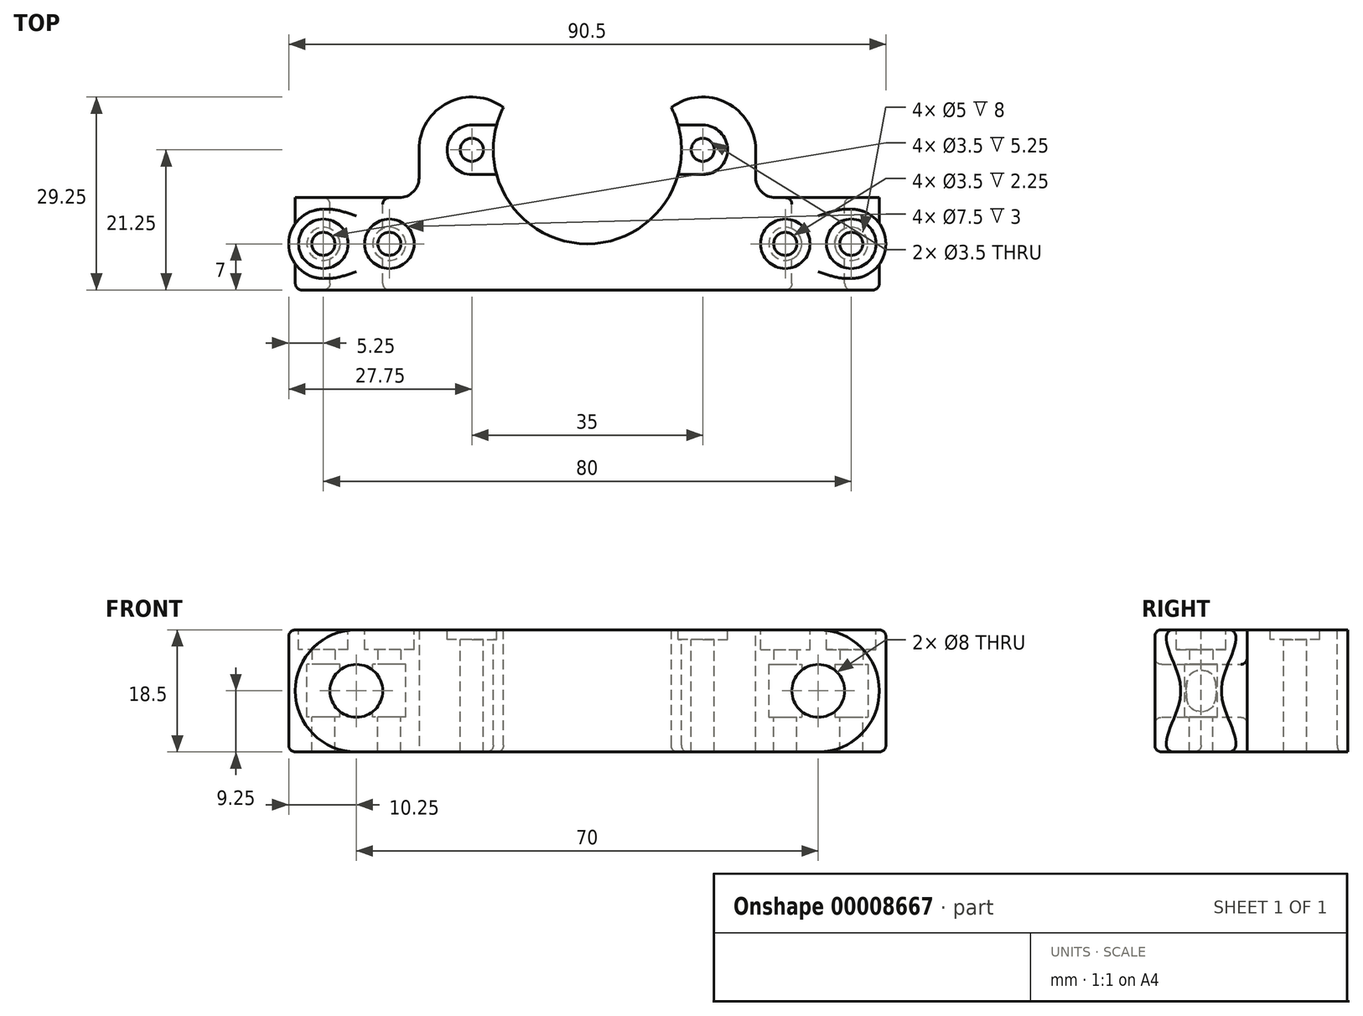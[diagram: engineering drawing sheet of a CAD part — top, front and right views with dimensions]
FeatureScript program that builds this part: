
annotation { "Feature Type Name" : "Feature", "Feature Type Description" : "" }
export const myFeature = defineFeature(function(context is Context, id is Id, definition is map)
    precondition{}
    {
        {
            var Q0;
            Q0=qCreatedBy(makeId("Front.planeOp"),FACE);
            var sketch = newSketch(context, id + "F0", { "sketchPlane" : qUnion([Q0])});
            skCircle(sketch, "E0", {"center": v(-35, 0) * mm, "radius": 4 * mm});
            skCircle(sketch, "E1", {"center": v(-35, 0) * mm, "radius": 9.25 * mm});
            skLineSegment(sketch, "E2", {"start": v(-44.25, 0) * mm, "end": v(0, 0) * mm});
            skLineSegment(sketch, "E3", {"start": v(-35, 9.25) * mm, "end": v(0, 9.25) * mm});
            skLineSegment(sketch, "E4", {"start": v(0, 0) * mm, "end": v(0, 9.25) * mm});
            skCircle(sketch, "E5", {"center": v(-6, 0) * mm, "radius": 2.75 * mm});
            skPoint(sketch, "E6", {"position": v(-35, -9.25) * mm});
            skSolve(sketch);
        }
        {
            var Q0;
            {var subQ0=sQuery(id+"F0.wireOp",EDGE,"E2");var subQ1=sQuery(id+"F0.wireOp",EDGE,"E0");var subQ2=makeQuery(id+"F0.imprint","INTERSECT",VERTEX,{"disambiguationData":[OD(0.0)],"derivedFrom":[subQ1,subQ0]});Q0=makeQuery(id+"F0.imprint","IMPRINT",FACE,{"disambiguationData":[TD([[makeQuery(id+"F0.imprint","IMPRINT",EDGE,{"disambiguationData":[TD([[subQ2,1.0]])],"derivedFrom":subQ1}),-1.0]])]});}
            var Q1;
            {var subQ1=sQuery(id+"F0.wireOp",EDGE,"E3");Q1=makeQuery(id+"F0.imprint","IMPRINT",FACE,{"disambiguationData":[TD([[makeQuery(id+"F0.imprint","IMPRINT",EDGE,{"derivedFrom":subQ1}),-1.0]])]});}
            var Q2;
            {var subQ0=sQuery(id+"F0.wireOp",EDGE,"E2");var subQ1=sQuery(id+"F0.wireOp",EDGE,"E0");var subQ3=makeQuery(id+"F0.imprint","INTERSECT",VERTEX,{"disambiguationData":[OD(0.0)],"derivedFrom":[subQ1,subQ0]});Q2=makeQuery(id+"F0.imprint","IMPRINT",FACE,{"disambiguationData":[TD([[makeQuery(id+"F0.imprint","IMPRINT",EDGE,{"disambiguationData":[TD([[subQ3,1.0]])],"derivedFrom":subQ1}),1.0]])]});}
            var Q3;
            {var subQ0=sQuery(id+"F0.wireOp",EDGE,"E5");var subQ1=sQuery(id+"F0.wireOp",EDGE,"E2");var subQ3=makeQuery(id+"F0.imprint","INTERSECT",VERTEX,{"disambiguationData":[OD(0.0)],"derivedFrom":[subQ1,subQ0]});Q3=makeQuery(id+"F0.imprint","IMPRINT",FACE,{"disambiguationData":[TD([[makeQuery(id+"F0.imprint","IMPRINT",EDGE,{"disambiguationData":[TD([[subQ3,-1.0]])],"derivedFrom":subQ1}),1.0]])]});}
            extrude(context, id + "F1", {"entities" : qUnion([Q0, Q1, Q2, Q3]), "depth" : 14 * mm, "symmetric" : true});
        }
        {
            var Q0;
            Q0=qCreatedBy(makeId("Top.planeOp"),FACE);
            var sketch = newSketch(context, id + "F2", { "sketchPlane" : qUnion([Q0])});
            skLineSegment(sketch, "E7.0", {"start": v(-31, 0) * mm, "end": v(-39, 0) * mm, "construction": true});
            skLineSegment(sketch, "E8.0", {"start": v(-35, 7) * mm, "end": v(-44.25, 7) * mm, "construction": true});
            skLineSegment(sketch, "E9.0", {"start": v(-35, -7) * mm, "end": v(-44.25, -7) * mm, "construction": true});
            skLineSegment(sketch, "E10.0", {"start": v(-35, -7) * mm, "end": v(0, -7) * mm, "construction": true});
            skLineSegment(sketch, "E11.0", {"start": v(-35, 7) * mm, "end": v(0, 7) * mm, "construction": true});
            skLineSegment(sketch, "E12", {"start": v(-39, 7) * mm, "end": v(-39, -7) * mm, "construction": true});
            skLineSegment(sketch, "E13", {"start": v(-31, 7) * mm, "end": v(-31, -7) * mm, "construction": true});
            skLineSegment(sketch, "E14", {"start": v(-35, 7) * mm, "end": v(-35, -7) * mm, "construction": true});
            skCircle(sketch, "E15", {"center": v(-40, 0) * mm, "radius": 1.75 * mm});
            skCircle(sketch, "E16", {"center": v(-30, 0) * mm, "radius": 1.75 * mm});
            skCircle(sketch, "E17", {"center": v(-30, 0) * mm, "radius": 2.5 * mm});
            skCircle(sketch, "E18", {"center": v(-40, 0) * mm, "radius": 2.5 * mm});
            skPoint(sketch, "E19", {"position": v(-38.25, 0) * mm});
            skCircle(sketch, "E20", {"center": v(-40, 0) * mm, "radius": 5.25 * mm});
            skCircle(sketch, "E21", {"center": v(-30, 0) * mm, "radius": 5.25 * mm});
            skCircle(sketch, "E22", {"center": v(-40, 0) * mm, "radius": 3.75 * mm});
            skCircle(sketch, "E23", {"center": v(-30, 0) * mm, "radius": 3.75 * mm});
            skLineSegment(sketch, "E24", {"start": v(-40, -5.25) * mm, "end": v(-35, -5.25) * mm});
            skLineSegment(sketch, "E25", {"start": v(-40, 5.25) * mm, "end": v(-35, 5.25) * mm});
            skLineSegment(sketch, "E26", {"start": v(-35, 5.25) * mm, "end": v(-35, -5.25) * mm});
            skSolve(sketch);
        }
        {
            var Q0;
            Q0=makeQuery(id+"F2.imprint","IMPRINT",FACE,{"disambiguationData":[TD([[makeQuery(id+"F2.imprint","IMPRINT",EDGE,{"derivedFrom":sQuery(id+"F2.wireOp",EDGE,"E20")}),1.0]])]});
            var Q1;
            Q1=makeQuery(id+"F2.imprint","IMPRINT",FACE,{"disambiguationData":[TD([[makeQuery(id+"F2.imprint","IMPRINT",EDGE,{"derivedFrom":sQuery(id+"F2.wireOp",EDGE,"E21")}),1.0]])]});
            var Q2;
            Q2=makeQuery(id+"F2.imprint","IMPRINT",FACE,{"disambiguationData":[TD([[makeQuery(id+"F2.imprint","IMPRINT",EDGE,{"derivedFrom":sQuery(id+"F2.wireOp",EDGE,"E18")}),-1.0]])]});
            var Q3;
            Q3=makeQuery(id+"F2.imprint","IMPRINT",FACE,{"disambiguationData":[TD([[makeQuery(id+"F2.imprint","IMPRINT",EDGE,{"derivedFrom":sQuery(id+"F2.wireOp",EDGE,"E15")}),-1.0]])]});
            var Q4;
            Q4=makeQuery(id+"F2.imprint","IMPRINT",FACE,{"disambiguationData":[TD([[makeQuery(id+"F2.imprint","IMPRINT",EDGE,{"derivedFrom":sQuery(id+"F2.wireOp",EDGE,"E15")}),1.0]])]});
            var Q5;
            Q5=makeQuery(id+"F2.imprint","IMPRINT",FACE,{"disambiguationData":[TD([[makeQuery(id+"F2.imprint","IMPRINT",EDGE,{"derivedFrom":sQuery(id+"F2.wireOp",EDGE,"E16")}),1.0]])]});
            var Q6;
            Q6=makeQuery(id+"F2.imprint","IMPRINT",FACE,{"disambiguationData":[TD([[makeQuery(id+"F2.imprint","IMPRINT",EDGE,{"derivedFrom":sQuery(id+"F2.wireOp",EDGE,"E16")}),-1.0]])]});
            var Q7;
            Q7=makeQuery(id+"F2.imprint","IMPRINT",FACE,{"disambiguationData":[TD([[makeQuery(id+"F2.imprint","IMPRINT",EDGE,{"derivedFrom":sQuery(id+"F2.wireOp",EDGE,"E17")}),-1.0]])]});
            var Q8;
            {var subQ3=sQuery(id+"F2.wireOp",EDGE,"E24");Q8=makeQuery(id+"F2.imprint","IMPRINT",FACE,{"disambiguationData":[TD([[makeQuery(id+"F2.imprint","IMPRINT",EDGE,{"derivedFrom":subQ3}),1.0]])]});}
            var Q9;
            {var subQ3=sQuery(id+"F2.wireOp",EDGE,"E25");Q9=makeQuery(id+"F2.imprint","IMPRINT",FACE,{"disambiguationData":[TD([[makeQuery(id+"F2.imprint","IMPRINT",EDGE,{"derivedFrom":subQ3}),-1.0]])]});}
            var Q10;
            Q10=makeQuery(id+"F1.opExtrude","SWEPT_FACE",FACE,{"disambiguationData":[OSD([sQuery(id+"F0.wireOp",EDGE,"E3")])]});
            extrude(context, id + "F3", {"entities" : qUnion([Q0, Q1, Q2, Q3, Q4, Q5, Q6, Q7, Q8, Q9]), "operationType" : NewBodyOperationType.ADD, "endBound" : BoundingType.UP_TO_SURFACE, "endBoundEntityFace" : qUnion([Q10]), "depth" : 8.5 * mm});
        }
        {
            var Q0;
            Q0=makeQuery(id+"F2.imprint","IMPRINT",FACE,{"disambiguationData":[TD([[makeQuery(id+"F2.imprint","IMPRINT",EDGE,{"derivedFrom":sQuery(id+"F2.wireOp",EDGE,"E15")}),1.0]])]});
            var Q1;
            Q1=makeQuery(id+"F2.imprint","IMPRINT",FACE,{"disambiguationData":[TD([[makeQuery(id+"F2.imprint","IMPRINT",EDGE,{"derivedFrom":sQuery(id+"F2.wireOp",EDGE,"E16")}),1.0]])]});
            extrude(context, id + "F4", {"entities" : qUnion([Q0, Q1]), "operationType" : NewBodyOperationType.REMOVE, "depth" : 25 * mm});
        }
        {
            var Q0;
            Q0=makeQuery(id+"F2.imprint","IMPRINT",FACE,{"disambiguationData":[TD([[makeQuery(id+"F2.imprint","IMPRINT",EDGE,{"derivedFrom":sQuery(id+"F2.wireOp",EDGE,"E15")}),-1.0]])]});
            var Q1;
            Q1=makeQuery(id+"F2.imprint","IMPRINT",FACE,{"disambiguationData":[TD([[makeQuery(id+"F2.imprint","IMPRINT",EDGE,{"derivedFrom":sQuery(id+"F2.wireOp",EDGE,"E15")}),1.0]])]});
            var Q2;
            Q2=makeQuery(id+"F2.imprint","IMPRINT",FACE,{"disambiguationData":[TD([[makeQuery(id+"F2.imprint","IMPRINT",EDGE,{"derivedFrom":sQuery(id+"F2.wireOp",EDGE,"E16")}),1.0]])]});
            var Q3;
            Q3=makeQuery(id+"F2.imprint","IMPRINT",FACE,{"disambiguationData":[TD([[makeQuery(id+"F2.imprint","IMPRINT",EDGE,{"derivedFrom":sQuery(id+"F2.wireOp",EDGE,"E16")}),-1.0]])]});
            extrude(context, id + "F5", {"entities" : qUnion([Q0, Q1, Q2, Q3]), "operationType" : NewBodyOperationType.REMOVE, "depth" : 4 * mm});
        }
        {
            var Q0;
            {var subQ0=sQuery(id+"F0.wireOp",EDGE,"E2");var subQ1=sQuery(id+"F0.wireOp",EDGE,"E0");var subQ3=makeQuery(id+"F0.imprint","INTERSECT",VERTEX,{"disambiguationData":[OD(0.0)],"derivedFrom":[subQ1,subQ0]});Q0=makeQuery(id+"F0.imprint","IMPRINT",FACE,{"disambiguationData":[TD([[makeQuery(id+"F0.imprint","IMPRINT",EDGE,{"disambiguationData":[TD([[subQ3,1.0]])],"derivedFrom":subQ1}),1.0]])]});}
            extrude(context, id + "F6", {"entities" : qUnion([Q0]), "operationType" : NewBodyOperationType.REMOVE, "depth" : 25 * mm, "symmetric" : true});
        }
        {
            var Q0;
            Q0=makeQuery(id+"F1.opExtrude","SWEPT_BODY",BODY,{"disambiguationData":[OSD([sQuery(id+"F0.wireOp",EDGE,"E1"),sQuery(id+"F0.wireOp",EDGE,"E2"),sQuery(id+"F0.wireOp",EDGE,"E3"),sQuery(id+"F0.wireOp",EDGE,"E4")])]});
            var Q1;
            Q1=qCreatedBy(makeId("Top.planeOp"),FACE);
            mirror(context, id + "F7", {"entities" : qUnion([Q0]), "mirrorPlane" : qUnion([Q1])});
        }
        {
            var Q0;
            Q0=makeQuery(id+"F1.opExtrude","SWEPT_FACE",FACE,{"disambiguationData":[OSD([sQuery(id+"F0.wireOp",EDGE,"E3")])]});
            var sketch = newSketch(context, id + "F8", { "sketchPlane" : qUnion([Q0])});
            skCircle(sketch, "E27.0.0", {"center": v(-40, 0) * mm, "radius": 5.25 * mm});
            skCircle(sketch, "E28.0", {"center": v(-30, 0) * mm, "radius": 1.75 * mm});
            skCircle(sketch, "E29", {"center": v(-30, 0) * mm, "radius": 3.75 * mm});
            skCircle(sketch, "E30", {"center": v(-40, 0) * mm, "radius": 3.75 * mm});
            skSolve(sketch);
        }
        {
            var Q0;
            Q0=makeQuery(id+"F8.imprint","IMPRINT",FACE,{"disambiguationData":[TD([[makeQuery(id+"F8.imprint","IMPRINT",EDGE,{"derivedFrom":sQuery(id+"F8.wireOp",EDGE,"E30")}),1.0]])]});
            var Q1;
            Q1=makeQuery(id+"F8.imprint","IMPRINT",FACE,{"disambiguationData":[TD([[makeQuery(id+"F8.imprint","IMPRINT",EDGE,{"derivedFrom":sQuery(id+"F8.wireOp",EDGE,"E28.0")}),1.0]])]});
            extrude(context, id + "F9", {"entities" : qUnion([Q0, Q1]), "operationType" : NewBodyOperationType.REMOVE, "oppositeDirection" : true, "depth" : 3 * mm});
        }
        {
            var Q0;
            Q0=makeQuery(id+"F1.opExtrude","SWEPT_BODY",BODY,{"disambiguationData":[OSD([sQuery(id+"F0.wireOp",EDGE,"E1"),sQuery(id+"F0.wireOp",EDGE,"E2"),sQuery(id+"F0.wireOp",EDGE,"E3"),sQuery(id+"F0.wireOp",EDGE,"E4")])]});
            var Q1;
            Q1=makeQuery(id+"F7.opPattern","COPY",BODY,{"derivedFrom":makeQuery(id+"F1.opExtrude","SWEPT_BODY",BODY,{"disambiguationData":[OSD([sQuery(id+"F0.wireOp",EDGE,"E1"),sQuery(id+"F0.wireOp",EDGE,"E2"),sQuery(id+"F0.wireOp",EDGE,"E3"),sQuery(id+"F0.wireOp",EDGE,"E4")])]}),"instanceName":"1"});
            var Q2;
            Q2=qCreatedBy(makeId("Right.planeOp"),FACE);
            mirror(context, id + "F10", {"entities" : qUnion([Q0, Q1]), "mirrorPlane" : qUnion([Q2])});
        }
        {
            var Q0;
            Q0=makeQuery(id+"F7.opPattern","COPY",BODY,{"derivedFrom":makeQuery(id+"F1.opExtrude","SWEPT_BODY",BODY,{"disambiguationData":[OSD([sQuery(id+"F0.wireOp",EDGE,"E1"),sQuery(id+"F0.wireOp",EDGE,"E2"),sQuery(id+"F0.wireOp",EDGE,"E3"),sQuery(id+"F0.wireOp",EDGE,"E4")])]}),"instanceName":"1"});
            var Q1;
            Q1=makeQuery(id+"F10.opPattern","COPY",BODY,{"derivedFrom":makeQuery(id+"F1.opExtrude","SWEPT_BODY",BODY,{"disambiguationData":[OSD([sQuery(id+"F0.wireOp",EDGE,"E1"),sQuery(id+"F0.wireOp",EDGE,"E2"),sQuery(id+"F0.wireOp",EDGE,"E3"),sQuery(id+"F0.wireOp",EDGE,"E4")])]}),"instanceName":"1"});
            var Q2;
            Q2=makeQuery(id+"F1.opExtrude","SWEPT_BODY",BODY,{"disambiguationData":[OSD([sQuery(id+"F0.wireOp",EDGE,"E1"),sQuery(id+"F0.wireOp",EDGE,"E2"),sQuery(id+"F0.wireOp",EDGE,"E3"),sQuery(id+"F0.wireOp",EDGE,"E4")])]});
            var Q3;
            Q3=makeQuery(id+"F10.opPattern","COPY",BODY,{"derivedFrom":makeQuery(id+"F7.opPattern","COPY",BODY,{"derivedFrom":makeQuery(id+"F1.opExtrude","SWEPT_BODY",BODY,{"disambiguationData":[OSD([sQuery(id+"F0.wireOp",EDGE,"E1"),sQuery(id+"F0.wireOp",EDGE,"E2"),sQuery(id+"F0.wireOp",EDGE,"E3"),sQuery(id+"F0.wireOp",EDGE,"E4")])]}),"instanceName":"1"}),"instanceName":"1"});
            booleanBodies(context, id + "F11", {"operationType" : BooleanOperationType.UNION, "tools" : qUnion([Q0, Q1, Q2, Q3])});
        }
        {
            var Q0;
            {var subQ0=sQuery(id+"F0.wireOp",EDGE,"E3");var subQ1=makeQuery(id+"F3.boolean.opBoolean","MERGE",FACE,{"derivedFrom":[makeQuery(id+"F1.opExtrude","SWEPT_FACE",FACE,{"disambiguationData":[OSD([subQ0])]}),makeQuery(id+"F3.opExtrude","CAP_FACE",FACE,{"disambiguationData":[OSD([subQ0]),ownerDisambiguation([makeQuery(id+"F3.opExtrude","SWEPT_BODY",BODY,{"disambiguationData":[OSD([sQuery(id+"F2.wireOp",EDGE,"E20"),sQuery(id+"F2.wireOp",EDGE,"E24"),sQuery(id+"F2.wireOp",EDGE,"E25"),sQuery(id+"F2.wireOp",EDGE,"E26")])]})])],"isStart":false})]});Q0=makeQuery(id+"F11.opBoolean","MERGE",FACE,{"derivedFrom":[subQ1,makeQuery(id+"F10.opPattern","COPY",FACE,{"derivedFrom":subQ1,"instanceName":"1"})]});}
            var sketch = newSketch(context, id + "F12", { "sketchPlane" : qUnion([Q0])});
            skCircle(sketch, "E31", {"center": v(-17.5, 14.25) * mm, "radius": 1.75 * mm});
            skCircle(sketch, "E32", {"center": v(17.5, 14.25) * mm, "radius": 1.75 * mm});
            skCircle(sketch, "E33", {"center": v(-17.5, 14.25) * mm, "radius": 3.75 * mm});
            skCircle(sketch, "E34", {"center": v(17.5, 14.25) * mm, "radius": 3.75 * mm});
            skCircle(sketch, "E35", {"center": v(0, 14.25) * mm, "radius": 14.25 * mm});
            skCircle(sketch, "E36", {"center": v(-17.5, 14.25) * mm, "radius": 8 * mm});
            skCircle(sketch, "E37", {"center": v(17.5, 14.25) * mm, "radius": 8 * mm});
            skLineSegment(sketch, "E38", {"start": v(-25.5, 14.25) * mm, "end": v(25.5, 14.25) * mm, "construction": true});
            skLineSegment(sketch, "E39", {"start": v(-25.5, 14.25) * mm, "end": v(-25.5, 0) * mm});
            skLineSegment(sketch, "E40", {"start": v(-25.5, 0) * mm, "end": v(25.5, 0) * mm});
            skLineSegment(sketch, "E41", {"start": v(25.5, 0) * mm, "end": v(25.5, 14.25) * mm});
            skLineSegment(sketch, "E42", {"start": v(-17.5, 22.25) * mm, "end": v(17.5, 22.25) * mm});
            skLineSegment(sketch, "E43", {"start": v(-17.5, 18) * mm, "end": v(17.5, 18) * mm});
            skLineSegment(sketch, "E44", {"start": v(17.5, 10.5) * mm, "end": v(-17.5, 10.5) * mm});
            skPoint(sketch, "E45", {"position": v(-11.8, 22.25) * mm});
            skPoint(sketch, "E46", {"position": v(11.8, 22.25) * mm});
            skSolve(sketch);
        }
        {
            var Q0;
            {var subQ7=sQuery(id+"F12.wireOp",EDGE,"E41");var subQ9=sQuery(id+"F12.wireOp",EDGE,"E40");var subQ10=makeQuery(id+"F12.imprint","INTERSECT",VERTEX,{"derivedFrom":[subQ9,subQ7]});Q0=makeQuery(id+"F12.imprint","IMPRINT",FACE,{"disambiguationData":[TD([[makeQuery(id+"F12.imprint","IMPRINT",EDGE,{"disambiguationData":[TD([[subQ10,1.0]])],"derivedFrom":subQ9}),1.0]])]});}
            var Q1;
            {var subQ0=sQuery(id+"F12.wireOp",EDGE,"E44");var subQ3=sQuery(id+"F12.wireOp",EDGE,"E35");var subQ4=makeQuery(id+"F12.imprint","INTERSECT",VERTEX,{"disambiguationData":[OD(0.0)],"derivedFrom":[subQ3,subQ0]});Q1=makeQuery(id+"F12.imprint","IMPRINT",FACE,{"disambiguationData":[TD([[makeQuery(id+"F12.imprint","IMPRINT",EDGE,{"disambiguationData":[TD([[subQ4,-1.0]])],"derivedFrom":subQ3}),1.0]])]});}
            var Q2;
            {var subQ0=sQuery(id+"F12.wireOp",EDGE,"E43");var subQ3=sQuery(id+"F12.wireOp",EDGE,"E33");var subQ4=makeQuery(id+"F12.imprint","INTERSECT",VERTEX,{"derivedFrom":[subQ3,subQ0]});Q2=makeQuery(id+"F12.imprint","IMPRINT",FACE,{"disambiguationData":[TD([[makeQuery(id+"F12.imprint","IMPRINT",EDGE,{"disambiguationData":[TD([[subQ4,1.0]])],"derivedFrom":subQ3}),-1.0]])]});}
            var Q3;
            {var subQ0=sQuery(id+"F12.wireOp",EDGE,"E42");var subQ1=sQuery(id+"F12.wireOp",EDGE,"E35");var subQ2=makeQuery(id+"F12.imprint","INTERSECT",VERTEX,{"disambiguationData":[OD(1.0)],"derivedFrom":[subQ1,subQ0]});Q3=makeQuery(id+"F12.imprint","IMPRINT",FACE,{"disambiguationData":[TD([[makeQuery(id+"F12.imprint","IMPRINT",EDGE,{"disambiguationData":[TD([[subQ2,-1.0]])],"derivedFrom":subQ1}),-1.0]])]});}
            var Q4;
            {var subQ0=sQuery(id+"F12.wireOp",EDGE,"E44");var subQ3=sQuery(id+"F12.wireOp",EDGE,"E34");var subQ4=makeQuery(id+"F12.imprint","INTERSECT",VERTEX,{"derivedFrom":[subQ3,subQ0]});Q4=makeQuery(id+"F12.imprint","IMPRINT",FACE,{"disambiguationData":[TD([[makeQuery(id+"F12.imprint","IMPRINT",EDGE,{"disambiguationData":[TD([[subQ4,1.0]])],"derivedFrom":subQ3}),-1.0]])]});}
            var Q5;
            {var subQ3=sQuery(id+"F12.wireOp",EDGE,"E35");var subQ8=sQuery(id+"F12.wireOp",EDGE,"E33");var subQ10=makeQuery(id+"F12.imprint","INTERSECT",VERTEX,{"disambiguationData":[OD(0.0)],"derivedFrom":[subQ8,subQ3]});Q5=makeQuery(id+"F12.imprint","IMPRINT",FACE,{"disambiguationData":[TD([[makeQuery(id+"F12.imprint","IMPRINT",EDGE,{"disambiguationData":[TD([[subQ10,1.0]])],"derivedFrom":subQ8}),-1.0]])]});}
            var Q6;
            {var subQ0=sQuery(id+"F12.wireOp",EDGE,"E44");var subQ3=sQuery(id+"F12.wireOp",EDGE,"E33");var subQ4=makeQuery(id+"F12.imprint","INTERSECT",VERTEX,{"derivedFrom":[subQ3,subQ0]});Q6=makeQuery(id+"F12.imprint","IMPRINT",FACE,{"disambiguationData":[TD([[makeQuery(id+"F12.imprint","IMPRINT",EDGE,{"disambiguationData":[TD([[subQ4,-1.0]])],"derivedFrom":subQ3}),-1.0]])]});}
            var Q7;
            {var subQ8=sQuery(id+"F12.wireOp",EDGE,"E33");var subQ10=sQuery(id+"F12.wireOp",EDGE,"E43");var subQ12=makeQuery(id+"F12.imprint","INTERSECT",VERTEX,{"derivedFrom":[subQ8,subQ10]});Q7=makeQuery(id+"F12.imprint","IMPRINT",FACE,{"disambiguationData":[TD([[makeQuery(id+"F12.imprint","IMPRINT",EDGE,{"disambiguationData":[TD([[subQ12,-1.0]])],"derivedFrom":subQ8}),-1.0]])]});}
            var Q8;
            Q8=makeQuery(id+"F12.imprint","IMPRINT",FACE,{"disambiguationData":[TD([[makeQuery(id+"F12.imprint","IMPRINT",EDGE,{"derivedFrom":sQuery(id+"F12.wireOp",EDGE,"E31")}),-1.0]])]});
            var Q9;
            {var subQ3=sQuery(id+"F12.wireOp",EDGE,"E35");var subQ8=sQuery(id+"F12.wireOp",EDGE,"E34");var subQ10=makeQuery(id+"F12.imprint","INTERSECT",VERTEX,{"disambiguationData":[OD(0.0)],"derivedFrom":[subQ8,subQ3]});Q9=makeQuery(id+"F12.imprint","IMPRINT",FACE,{"disambiguationData":[TD([[makeQuery(id+"F12.imprint","IMPRINT",EDGE,{"disambiguationData":[TD([[subQ10,-1.0]])],"derivedFrom":subQ8}),-1.0]])]});}
            var Q10;
            {var subQ5=sQuery(id+"F12.wireOp",EDGE,"E42");var subQ6=sQuery(id+"F12.wireOp",EDGE,"E35");var subQ8=makeQuery(id+"F12.imprint","INTERSECT",VERTEX,{"disambiguationData":[OD(0.0)],"derivedFrom":[subQ6,subQ5]});Q10=makeQuery(id+"F12.imprint","IMPRINT",FACE,{"disambiguationData":[TD([[makeQuery(id+"F12.imprint","IMPRINT",EDGE,{"disambiguationData":[TD([[subQ8,1.0]])],"derivedFrom":subQ6}),1.0]])]});}
            var Q11;
            {var subQ2=sQuery(id+"F12.wireOp",EDGE,"E37");var subQ4=sQuery(id+"F12.wireOp",EDGE,"E35");var subQ6=makeQuery(id+"F12.imprint","INTERSECT",VERTEX,{"disambiguationData":[OD(1.0)],"derivedFrom":[subQ4,subQ2]});Q11=makeQuery(id+"F12.imprint","IMPRINT",FACE,{"disambiguationData":[TD([[makeQuery(id+"F12.imprint","IMPRINT",EDGE,{"disambiguationData":[TD([[subQ6,1.0]])],"derivedFrom":subQ4}),-1.0]])]});}
            var Q12;
            {var subQ2=sQuery(id+"F12.wireOp",EDGE,"E36");var subQ4=sQuery(id+"F12.wireOp",EDGE,"E39");var subQ6=makeQuery(id+"F12.imprint","INTERSECT",VERTEX,{"derivedFrom":[subQ2,subQ4]});Q12=makeQuery(id+"F12.imprint","IMPRINT",FACE,{"disambiguationData":[TD([[makeQuery(id+"F12.imprint","IMPRINT",EDGE,{"disambiguationData":[TD([[subQ6,-1.0]])],"derivedFrom":subQ2}),-1.0]])]});}
            var Q13;
            {var subQ0=makeQuery(id+"F1.opExtrude","CAP_EDGE",EDGE,{"disambiguationData":[OSD([sQuery(id+"F0.wireOp",EDGE,"E3")])],"isStart":true});var subQ1=makeQuery(id+"F11.opBoolean","MERGE",EDGE,{"derivedFrom":[subQ0,makeQuery(id+"F10.opPattern","COPY",EDGE,{"derivedFrom":subQ0,"instanceName":"1"})]});var subQ2=sQuery(id+"F12.wireOp",EDGE,"E36");var subQ4=makeQuery(id+"F12.imprint","INTERSECT",VERTEX,{"disambiguationData":[OD(0.0)],"derivedFrom":[subQ1,subQ2]});Q13=makeQuery(id+"F12.imprint","IMPRINT",FACE,{"disambiguationData":[TD([[makeQuery(id+"F12.imprint","IMPRINT",EDGE,{"disambiguationData":[TD([[subQ4,-1.0]])],"derivedFrom":subQ2}),1.0]])]});}
            var Q14;
            {var subQ0=makeQuery(id+"F1.opExtrude","CAP_EDGE",EDGE,{"disambiguationData":[OSD([sQuery(id+"F0.wireOp",EDGE,"E3")])],"isStart":true});var subQ1=makeQuery(id+"F11.opBoolean","MERGE",EDGE,{"derivedFrom":[subQ0,makeQuery(id+"F10.opPattern","COPY",EDGE,{"derivedFrom":subQ0,"instanceName":"1"})]});var subQ2=sQuery(id+"F12.wireOp",EDGE,"E37");var subQ4=makeQuery(id+"F12.imprint","INTERSECT",VERTEX,{"disambiguationData":[OD(0.0)],"derivedFrom":[subQ1,subQ2]});Q14=makeQuery(id+"F12.imprint","IMPRINT",FACE,{"disambiguationData":[TD([[makeQuery(id+"F12.imprint","IMPRINT",EDGE,{"disambiguationData":[TD([[subQ4,-1.0]])],"derivedFrom":subQ2}),1.0]])]});}
            var Q15;
            {var subQ2=sQuery(id+"F12.wireOp",EDGE,"E37");var subQ4=sQuery(id+"F12.wireOp",EDGE,"E41");var subQ6=makeQuery(id+"F12.imprint","INTERSECT",VERTEX,{"derivedFrom":[subQ2,subQ4]});Q15=makeQuery(id+"F12.imprint","IMPRINT",FACE,{"disambiguationData":[TD([[makeQuery(id+"F12.imprint","IMPRINT",EDGE,{"disambiguationData":[TD([[subQ6,1.0]])],"derivedFrom":subQ2}),-1.0]])]});}
            var Q16;
            {var subQ2=sQuery(id+"F12.wireOp",EDGE,"E35");var subQ5=makeQuery(id+"F12.imprint","INTERSECT",VERTEX,{"derivedFrom":[subQ2,sQuery(id+"F12.wireOp",EDGE,"E40")]});Q16=makeQuery(id+"F12.imprint","IMPRINT",FACE,{"disambiguationData":[TD([[makeQuery(id+"F12.imprint","IMPRINT",EDGE,{"disambiguationData":[TD([[subQ5,1.0]])],"derivedFrom":subQ2}),1.0]])]});}
            var Q17;
            {var subQ2=sQuery(id+"F12.wireOp",EDGE,"E36");var subQ4=sQuery(id+"F12.wireOp",EDGE,"E35");var subQ6=makeQuery(id+"F12.imprint","INTERSECT",VERTEX,{"disambiguationData":[OD(1.0)],"derivedFrom":[subQ4,subQ2]});Q17=makeQuery(id+"F12.imprint","IMPRINT",FACE,{"disambiguationData":[TD([[makeQuery(id+"F12.imprint","IMPRINT",EDGE,{"disambiguationData":[TD([[subQ6,-1.0]])],"derivedFrom":subQ4}),-1.0]])]});}
            var Q18;
            {var subQ0=sQuery(id+"F12.wireOp",EDGE,"E43");var subQ3=sQuery(id+"F12.wireOp",EDGE,"E35");var subQ4=makeQuery(id+"F12.imprint","INTERSECT",VERTEX,{"disambiguationData":[OD(0.0)],"derivedFrom":[subQ3,subQ0]});Q18=makeQuery(id+"F12.imprint","IMPRINT",FACE,{"disambiguationData":[TD([[makeQuery(id+"F12.imprint","IMPRINT",EDGE,{"disambiguationData":[TD([[subQ4,-1.0]])],"derivedFrom":subQ3}),1.0]])]});}
            var Q19;
            {var subQ0=sQuery(id+"F12.wireOp",EDGE,"E43");var subQ3=sQuery(id+"F12.wireOp",EDGE,"E34");var subQ4=makeQuery(id+"F12.imprint","INTERSECT",VERTEX,{"derivedFrom":[subQ3,subQ0]});Q19=makeQuery(id+"F12.imprint","IMPRINT",FACE,{"disambiguationData":[TD([[makeQuery(id+"F12.imprint","IMPRINT",EDGE,{"disambiguationData":[TD([[subQ4,-1.0]])],"derivedFrom":subQ3}),-1.0]])]});}
            var Q20;
            {var subQ1=sQuery(id+"F12.wireOp",EDGE,"E37");var subQ3=sQuery(id+"F12.wireOp",EDGE,"E35");var subQ5=makeQuery(id+"F12.imprint","INTERSECT",VERTEX,{"disambiguationData":[OD(1.0)],"derivedFrom":[subQ3,subQ1]});Q20=makeQuery(id+"F12.imprint","IMPRINT",FACE,{"disambiguationData":[TD([[makeQuery(id+"F12.imprint","IMPRINT",EDGE,{"disambiguationData":[TD([[subQ5,-1.0]])],"derivedFrom":subQ3}),1.0]])]});}
            var Q21;
            {var subQ8=sQuery(id+"F12.wireOp",EDGE,"E34");var subQ10=sQuery(id+"F12.wireOp",EDGE,"E43");var subQ12=makeQuery(id+"F12.imprint","INTERSECT",VERTEX,{"derivedFrom":[subQ8,subQ10]});Q21=makeQuery(id+"F12.imprint","IMPRINT",FACE,{"disambiguationData":[TD([[makeQuery(id+"F12.imprint","IMPRINT",EDGE,{"disambiguationData":[TD([[subQ12,1.0]])],"derivedFrom":subQ8}),-1.0]])]});}
            var Q22;
            {var subQ3=sQuery(id+"F12.wireOp",EDGE,"E36");var subQ5=sQuery(id+"F12.wireOp",EDGE,"E43");var subQ7=makeQuery(id+"F12.imprint","INTERSECT",VERTEX,{"derivedFrom":[subQ3,subQ5]});Q22=makeQuery(id+"F12.imprint","IMPRINT",FACE,{"disambiguationData":[TD([[makeQuery(id+"F12.imprint","IMPRINT",EDGE,{"disambiguationData":[TD([[subQ7,1.0]])],"derivedFrom":subQ3}),-1.0]])]});}
            var Q23;
            {var subQ7=sQuery(id+"F12.wireOp",EDGE,"E39");var subQ9=sQuery(id+"F12.wireOp",EDGE,"E40");var subQ11=makeQuery(id+"F12.imprint","INTERSECT",VERTEX,{"derivedFrom":[subQ7,subQ9]});Q23=makeQuery(id+"F12.imprint","IMPRINT",FACE,{"disambiguationData":[TD([[makeQuery(id+"F12.imprint","IMPRINT",EDGE,{"disambiguationData":[TD([[subQ11,-1.0]])],"derivedFrom":subQ9}),1.0]])]});}
            var Q24;
            Q24=makeQuery(id+"F12.imprint","IMPRINT",FACE,{"disambiguationData":[TD([[makeQuery(id+"F12.imprint","IMPRINT",EDGE,{"derivedFrom":sQuery(id+"F12.wireOp",EDGE,"E32")}),1.0]])]});
            var Q25;
            {var subQ0=sQuery(id+"F12.wireOp",EDGE,"E42");var subQ1=sQuery(id+"F12.wireOp",EDGE,"E35");var subQ3=makeQuery(id+"F12.imprint","INTERSECT",VERTEX,{"disambiguationData":[OD(0.0)],"derivedFrom":[subQ1,subQ0]});Q25=makeQuery(id+"F12.imprint","IMPRINT",FACE,{"disambiguationData":[TD([[makeQuery(id+"F12.imprint","IMPRINT",EDGE,{"disambiguationData":[TD([[subQ3,-1.0]])],"derivedFrom":subQ1}),1.0]])]});}
            var Q26;
            {var subQ2=sQuery(id+"F12.wireOp",EDGE,"E35");var subQ8=sQuery(id+"F12.wireOp",EDGE,"E36");var subQ11=makeQuery(id+"F12.imprint","INTERSECT",VERTEX,{"disambiguationData":[OD(1.0)],"derivedFrom":[subQ2,subQ8]});Q26=makeQuery(id+"F12.imprint","IMPRINT",FACE,{"disambiguationData":[TD([[makeQuery(id+"F12.imprint","IMPRINT",EDGE,{"disambiguationData":[TD([[subQ11,-1.0]])],"derivedFrom":subQ8}),-1.0]])]});}
            var Q27;
            {var subQ1=sQuery(id+"F12.wireOp",EDGE,"E36");var subQ3=sQuery(id+"F12.wireOp",EDGE,"E35");var subQ5=makeQuery(id+"F12.imprint","INTERSECT",VERTEX,{"disambiguationData":[OD(0.0)],"derivedFrom":[subQ3,subQ1]});Q27=makeQuery(id+"F12.imprint","IMPRINT",FACE,{"disambiguationData":[TD([[makeQuery(id+"F12.imprint","IMPRINT",EDGE,{"disambiguationData":[TD([[subQ5,-1.0]])],"derivedFrom":subQ3}),1.0]])]});}
            var Q28;
            Q28=makeQuery(id+"F12.imprint","IMPRINT",FACE,{"disambiguationData":[TD([[makeQuery(id+"F12.imprint","IMPRINT",EDGE,{"derivedFrom":sQuery(id+"F12.wireOp",EDGE,"E31")}),1.0]])]});
            var Q29;
            Q29=makeQuery(id+"F12.imprint","IMPRINT",FACE,{"disambiguationData":[TD([[makeQuery(id+"F12.imprint","IMPRINT",EDGE,{"derivedFrom":sQuery(id+"F12.wireOp",EDGE,"E32")}),-1.0]])]});
            var Q30;
            {var subQ0=sQuery(id+"F12.wireOp",EDGE,"E42");var subQ1=sQuery(id+"F12.wireOp",EDGE,"E35");var subQ2=makeQuery(id+"F12.imprint","INTERSECT",VERTEX,{"disambiguationData":[OD(0.0)],"derivedFrom":[subQ1,subQ0]});Q30=makeQuery(id+"F12.imprint","IMPRINT",FACE,{"disambiguationData":[TD([[makeQuery(id+"F12.imprint","IMPRINT",EDGE,{"disambiguationData":[TD([[subQ2,1.0]])],"derivedFrom":subQ1}),-1.0]])]});}
            var Q31;
            {var subQ0=sQuery(id+"F12.wireOp",EDGE,"E35");var subQ1=sQuery(id+"F12.wireOp",EDGE,"E33");var subQ3=makeQuery(id+"F12.imprint","INTERSECT",VERTEX,{"disambiguationData":[OD(0.0)],"derivedFrom":[subQ1,subQ0]});Q31=makeQuery(id+"F12.imprint","IMPRINT",FACE,{"disambiguationData":[TD([[makeQuery(id+"F12.imprint","IMPRINT",EDGE,{"disambiguationData":[TD([[subQ3,1.0]])],"derivedFrom":subQ1}),1.0]])]});}
            var Q32;
            {var subQ0=sQuery(id+"F12.wireOp",EDGE,"E35");var subQ1=sQuery(id+"F12.wireOp",EDGE,"E34");var subQ3=makeQuery(id+"F12.imprint","INTERSECT",VERTEX,{"disambiguationData":[OD(0.0)],"derivedFrom":[subQ1,subQ0]});Q32=makeQuery(id+"F12.imprint","IMPRINT",FACE,{"disambiguationData":[TD([[makeQuery(id+"F12.imprint","IMPRINT",EDGE,{"disambiguationData":[TD([[subQ3,-1.0]])],"derivedFrom":subQ1}),1.0]])]});}
            extrude(context, id + "F13", {"entities" : qUnion([Q0, Q1, Q2, Q3, Q4, Q5, Q6, Q7, Q8, Q9, Q10, Q11, Q12, Q13, Q14, Q15, Q16, Q17, Q18, Q19, Q20, Q21, Q22, Q23, Q24, Q25, Q26, Q27, Q28, Q29, Q30, Q31, Q32]), "operationType" : NewBodyOperationType.ADD, "oppositeDirection" : true, "depth" : 18.5 * mm});
        }
        {
            var Q0;
            {var subQ0=sQuery(id+"F12.wireOp",EDGE,"E43");var subQ3=sQuery(id+"F12.wireOp",EDGE,"E33");var subQ4=makeQuery(id+"F12.imprint","INTERSECT",VERTEX,{"derivedFrom":[subQ3,subQ0]});Q0=makeQuery(id+"F12.imprint","IMPRINT",FACE,{"disambiguationData":[TD([[makeQuery(id+"F12.imprint","IMPRINT",EDGE,{"disambiguationData":[TD([[subQ4,1.0]])],"derivedFrom":subQ3}),-1.0]])]});}
            var Q1;
            {var subQ0=sQuery(id+"F12.wireOp",EDGE,"E43");var subQ3=sQuery(id+"F12.wireOp",EDGE,"E35");var subQ4=makeQuery(id+"F12.imprint","INTERSECT",VERTEX,{"disambiguationData":[OD(0.0)],"derivedFrom":[subQ3,subQ0]});Q1=makeQuery(id+"F12.imprint","IMPRINT",FACE,{"disambiguationData":[TD([[makeQuery(id+"F12.imprint","IMPRINT",EDGE,{"disambiguationData":[TD([[subQ4,-1.0]])],"derivedFrom":subQ3}),1.0]])]});}
            var Q2;
            Q2=makeQuery(id+"F12.imprint","IMPRINT",FACE,{"disambiguationData":[TD([[makeQuery(id+"F12.imprint","IMPRINT",EDGE,{"derivedFrom":sQuery(id+"F12.wireOp",EDGE,"E32")}),-1.0]])]});
            var Q3;
            {var subQ0=sQuery(id+"F12.wireOp",EDGE,"E44");var subQ3=sQuery(id+"F12.wireOp",EDGE,"E35");var subQ4=makeQuery(id+"F12.imprint","INTERSECT",VERTEX,{"disambiguationData":[OD(0.0)],"derivedFrom":[subQ3,subQ0]});Q3=makeQuery(id+"F12.imprint","IMPRINT",FACE,{"disambiguationData":[TD([[makeQuery(id+"F12.imprint","IMPRINT",EDGE,{"disambiguationData":[TD([[subQ4,-1.0]])],"derivedFrom":subQ3}),1.0]])]});}
            var Q4;
            {var subQ4=sQuery(id+"F12.wireOp",EDGE,"E35");var subQ7=makeQuery(id+"F12.imprint","INTERSECT",VERTEX,{"derivedFrom":[subQ4,sQuery(id+"F12.wireOp",EDGE,"E40")]});Q4=makeQuery(id+"F12.imprint","IMPRINT",FACE,{"disambiguationData":[TD([[makeQuery(id+"F12.imprint","IMPRINT",EDGE,{"disambiguationData":[TD([[subQ7,1.0]])],"derivedFrom":subQ4}),1.0]])]});}
            var Q5;
            {var subQ1=sQuery(id+"F12.wireOp",EDGE,"E37");var subQ3=sQuery(id+"F12.wireOp",EDGE,"E35");var subQ5=makeQuery(id+"F12.imprint","INTERSECT",VERTEX,{"disambiguationData":[OD(1.0)],"derivedFrom":[subQ3,subQ1]});Q5=makeQuery(id+"F12.imprint","IMPRINT",FACE,{"disambiguationData":[TD([[makeQuery(id+"F12.imprint","IMPRINT",EDGE,{"disambiguationData":[TD([[subQ5,-1.0]])],"derivedFrom":subQ3}),1.0]])]});}
            var Q6;
            {var subQ3=sQuery(id+"F12.wireOp",EDGE,"E35");var subQ8=sQuery(id+"F12.wireOp",EDGE,"E33");var subQ10=makeQuery(id+"F12.imprint","INTERSECT",VERTEX,{"disambiguationData":[OD(0.0)],"derivedFrom":[subQ8,subQ3]});Q6=makeQuery(id+"F12.imprint","IMPRINT",FACE,{"disambiguationData":[TD([[makeQuery(id+"F12.imprint","IMPRINT",EDGE,{"disambiguationData":[TD([[subQ10,1.0]])],"derivedFrom":subQ8}),-1.0]])]});}
            var Q7;
            Q7=makeQuery(id+"F12.imprint","IMPRINT",FACE,{"disambiguationData":[TD([[makeQuery(id+"F12.imprint","IMPRINT",EDGE,{"derivedFrom":sQuery(id+"F12.wireOp",EDGE,"E32")}),1.0]])]});
            var Q8;
            {var subQ0=sQuery(id+"F12.wireOp",EDGE,"E43");var subQ3=sQuery(id+"F12.wireOp",EDGE,"E34");var subQ4=makeQuery(id+"F12.imprint","INTERSECT",VERTEX,{"derivedFrom":[subQ3,subQ0]});Q8=makeQuery(id+"F12.imprint","IMPRINT",FACE,{"disambiguationData":[TD([[makeQuery(id+"F12.imprint","IMPRINT",EDGE,{"disambiguationData":[TD([[subQ4,-1.0]])],"derivedFrom":subQ3}),-1.0]])]});}
            var Q9;
            {var subQ3=sQuery(id+"F12.wireOp",EDGE,"E36");var subQ5=sQuery(id+"F12.wireOp",EDGE,"E43");var subQ7=makeQuery(id+"F12.imprint","INTERSECT",VERTEX,{"derivedFrom":[subQ3,subQ5]});Q9=makeQuery(id+"F12.imprint","IMPRINT",FACE,{"disambiguationData":[TD([[makeQuery(id+"F12.imprint","IMPRINT",EDGE,{"disambiguationData":[TD([[subQ7,1.0]])],"derivedFrom":subQ3}),-1.0]])]});}
            var Q10;
            {var subQ0=sQuery(id+"F12.wireOp",EDGE,"E44");var subQ3=sQuery(id+"F12.wireOp",EDGE,"E34");var subQ4=makeQuery(id+"F12.imprint","INTERSECT",VERTEX,{"derivedFrom":[subQ3,subQ0]});Q10=makeQuery(id+"F12.imprint","IMPRINT",FACE,{"disambiguationData":[TD([[makeQuery(id+"F12.imprint","IMPRINT",EDGE,{"disambiguationData":[TD([[subQ4,1.0]])],"derivedFrom":subQ3}),-1.0]])]});}
            var Q11;
            {var subQ0=sQuery(id+"F12.wireOp",EDGE,"E44");var subQ3=sQuery(id+"F12.wireOp",EDGE,"E33");var subQ4=makeQuery(id+"F12.imprint","INTERSECT",VERTEX,{"derivedFrom":[subQ3,subQ0]});Q11=makeQuery(id+"F12.imprint","IMPRINT",FACE,{"disambiguationData":[TD([[makeQuery(id+"F12.imprint","IMPRINT",EDGE,{"disambiguationData":[TD([[subQ4,-1.0]])],"derivedFrom":subQ3}),-1.0]])]});}
            var Q12;
            {var subQ3=sQuery(id+"F12.wireOp",EDGE,"E35");var subQ7=sQuery(id+"F12.wireOp",EDGE,"E34");var subQ10=makeQuery(id+"F12.imprint","INTERSECT",VERTEX,{"disambiguationData":[OD(0.0)],"derivedFrom":[subQ7,subQ3]});Q12=makeQuery(id+"F12.imprint","IMPRINT",FACE,{"disambiguationData":[TD([[makeQuery(id+"F12.imprint","IMPRINT",EDGE,{"disambiguationData":[TD([[subQ10,-1.0]])],"derivedFrom":subQ7}),-1.0]])]});}
            var Q13;
            Q13=makeQuery(id+"F12.imprint","IMPRINT",FACE,{"disambiguationData":[TD([[makeQuery(id+"F12.imprint","IMPRINT",EDGE,{"derivedFrom":sQuery(id+"F12.wireOp",EDGE,"E31")}),1.0]])]});
            var Q14;
            {var subQ1=sQuery(id+"F12.wireOp",EDGE,"E36");var subQ3=sQuery(id+"F12.wireOp",EDGE,"E35");var subQ5=makeQuery(id+"F12.imprint","INTERSECT",VERTEX,{"disambiguationData":[OD(0.0)],"derivedFrom":[subQ3,subQ1]});Q14=makeQuery(id+"F12.imprint","IMPRINT",FACE,{"disambiguationData":[TD([[makeQuery(id+"F12.imprint","IMPRINT",EDGE,{"disambiguationData":[TD([[subQ5,-1.0]])],"derivedFrom":subQ3}),1.0]])]});}
            var Q15;
            Q15=makeQuery(id+"F12.imprint","IMPRINT",FACE,{"disambiguationData":[TD([[makeQuery(id+"F12.imprint","IMPRINT",EDGE,{"derivedFrom":sQuery(id+"F12.wireOp",EDGE,"E31")}),-1.0]])]});
            var Q16;
            {var subQ0=sQuery(id+"F12.wireOp",EDGE,"E35");var subQ1=sQuery(id+"F12.wireOp",EDGE,"E34");var subQ3=makeQuery(id+"F12.imprint","INTERSECT",VERTEX,{"disambiguationData":[OD(0.0)],"derivedFrom":[subQ1,subQ0]});Q16=makeQuery(id+"F12.imprint","IMPRINT",FACE,{"disambiguationData":[TD([[makeQuery(id+"F12.imprint","IMPRINT",EDGE,{"disambiguationData":[TD([[subQ3,-1.0]])],"derivedFrom":subQ1}),1.0]])]});}
            var Q17;
            {var subQ0=sQuery(id+"F12.wireOp",EDGE,"E35");var subQ1=sQuery(id+"F12.wireOp",EDGE,"E33");var subQ3=makeQuery(id+"F12.imprint","INTERSECT",VERTEX,{"disambiguationData":[OD(0.0)],"derivedFrom":[subQ1,subQ0]});Q17=makeQuery(id+"F12.imprint","IMPRINT",FACE,{"disambiguationData":[TD([[makeQuery(id+"F12.imprint","IMPRINT",EDGE,{"disambiguationData":[TD([[subQ3,1.0]])],"derivedFrom":subQ1}),1.0]])]});}
            var Q18;
            {var subQ5=sQuery(id+"F12.wireOp",EDGE,"E42");var subQ6=sQuery(id+"F12.wireOp",EDGE,"E35");var subQ8=makeQuery(id+"F12.imprint","INTERSECT",VERTEX,{"disambiguationData":[OD(0.0)],"derivedFrom":[subQ6,subQ5]});Q18=makeQuery(id+"F12.imprint","IMPRINT",FACE,{"disambiguationData":[TD([[makeQuery(id+"F12.imprint","IMPRINT",EDGE,{"disambiguationData":[TD([[subQ8,1.0]])],"derivedFrom":subQ6}),1.0]])]});}
            var Q19;
            {var subQ4=sQuery(id+"F12.wireOp",EDGE,"E35");var subQ10=sQuery(id+"F12.wireOp",EDGE,"E36");var subQ13=makeQuery(id+"F12.imprint","INTERSECT",VERTEX,{"disambiguationData":[OD(1.0)],"derivedFrom":[subQ4,subQ10]});Q19=makeQuery(id+"F12.imprint","IMPRINT",FACE,{"disambiguationData":[TD([[makeQuery(id+"F12.imprint","IMPRINT",EDGE,{"disambiguationData":[TD([[subQ13,-1.0]])],"derivedFrom":subQ10}),-1.0]])]});}
            var Q20;
            {var subQ0=sQuery(id+"F12.wireOp",EDGE,"E42");var subQ1=sQuery(id+"F12.wireOp",EDGE,"E35");var subQ3=makeQuery(id+"F12.imprint","INTERSECT",VERTEX,{"disambiguationData":[OD(0.0)],"derivedFrom":[subQ1,subQ0]});Q20=makeQuery(id+"F12.imprint","IMPRINT",FACE,{"disambiguationData":[TD([[makeQuery(id+"F12.imprint","IMPRINT",EDGE,{"disambiguationData":[TD([[subQ3,-1.0]])],"derivedFrom":subQ1}),1.0]])]});}
            extrude(context, id + "F14", {"entities" : qUnion([Q0, Q1, Q2, Q3, Q4, Q5, Q6, Q7, Q8, Q9, Q10, Q11, Q12, Q13, Q14, Q15, Q16, Q17, Q18, Q19, Q20]), "operationType" : NewBodyOperationType.REMOVE, "oppositeDirection" : true, "depth" : 1.5 * mm});
        }
        {
            var Q0;
            {var subQ4=sQuery(id+"F12.wireOp",EDGE,"E35");var subQ10=sQuery(id+"F12.wireOp",EDGE,"E36");var subQ13=makeQuery(id+"F12.imprint","INTERSECT",VERTEX,{"disambiguationData":[OD(1.0)],"derivedFrom":[subQ4,subQ10]});Q0=makeQuery(id+"F12.imprint","IMPRINT",FACE,{"disambiguationData":[TD([[makeQuery(id+"F12.imprint","IMPRINT",EDGE,{"disambiguationData":[TD([[subQ13,-1.0]])],"derivedFrom":subQ10}),-1.0]])]});}
            var Q1;
            {var subQ4=sQuery(id+"F12.wireOp",EDGE,"E35");var subQ7=makeQuery(id+"F12.imprint","INTERSECT",VERTEX,{"derivedFrom":[subQ4,sQuery(id+"F12.wireOp",EDGE,"E40")]});Q1=makeQuery(id+"F12.imprint","IMPRINT",FACE,{"disambiguationData":[TD([[makeQuery(id+"F12.imprint","IMPRINT",EDGE,{"disambiguationData":[TD([[subQ7,1.0]])],"derivedFrom":subQ4}),1.0]])]});}
            var Q2;
            {var subQ1=sQuery(id+"F12.wireOp",EDGE,"E37");var subQ3=sQuery(id+"F12.wireOp",EDGE,"E35");var subQ5=makeQuery(id+"F12.imprint","INTERSECT",VERTEX,{"disambiguationData":[OD(1.0)],"derivedFrom":[subQ3,subQ1]});Q2=makeQuery(id+"F12.imprint","IMPRINT",FACE,{"disambiguationData":[TD([[makeQuery(id+"F12.imprint","IMPRINT",EDGE,{"disambiguationData":[TD([[subQ5,-1.0]])],"derivedFrom":subQ3}),1.0]])]});}
            var Q3;
            {var subQ3=sQuery(id+"F12.wireOp",EDGE,"E35");var subQ7=sQuery(id+"F12.wireOp",EDGE,"E34");var subQ10=makeQuery(id+"F12.imprint","INTERSECT",VERTEX,{"disambiguationData":[OD(0.0)],"derivedFrom":[subQ7,subQ3]});Q3=makeQuery(id+"F12.imprint","IMPRINT",FACE,{"disambiguationData":[TD([[makeQuery(id+"F12.imprint","IMPRINT",EDGE,{"disambiguationData":[TD([[subQ10,-1.0]])],"derivedFrom":subQ7}),-1.0]])]});}
            var Q4;
            {var subQ0=sQuery(id+"F12.wireOp",EDGE,"E43");var subQ3=sQuery(id+"F12.wireOp",EDGE,"E35");var subQ4=makeQuery(id+"F12.imprint","INTERSECT",VERTEX,{"disambiguationData":[OD(0.0)],"derivedFrom":[subQ3,subQ0]});Q4=makeQuery(id+"F12.imprint","IMPRINT",FACE,{"disambiguationData":[TD([[makeQuery(id+"F12.imprint","IMPRINT",EDGE,{"disambiguationData":[TD([[subQ4,-1.0]])],"derivedFrom":subQ3}),1.0]])]});}
            var Q5;
            {var subQ5=sQuery(id+"F12.wireOp",EDGE,"E42");var subQ6=sQuery(id+"F12.wireOp",EDGE,"E35");var subQ8=makeQuery(id+"F12.imprint","INTERSECT",VERTEX,{"disambiguationData":[OD(0.0)],"derivedFrom":[subQ6,subQ5]});Q5=makeQuery(id+"F12.imprint","IMPRINT",FACE,{"disambiguationData":[TD([[makeQuery(id+"F12.imprint","IMPRINT",EDGE,{"disambiguationData":[TD([[subQ8,1.0]])],"derivedFrom":subQ6}),1.0]])]});}
            var Q6;
            {var subQ3=sQuery(id+"F12.wireOp",EDGE,"E36");var subQ5=sQuery(id+"F12.wireOp",EDGE,"E43");var subQ7=makeQuery(id+"F12.imprint","INTERSECT",VERTEX,{"derivedFrom":[subQ3,subQ5]});Q6=makeQuery(id+"F12.imprint","IMPRINT",FACE,{"disambiguationData":[TD([[makeQuery(id+"F12.imprint","IMPRINT",EDGE,{"disambiguationData":[TD([[subQ7,1.0]])],"derivedFrom":subQ3}),-1.0]])]});}
            var Q7;
            {var subQ3=sQuery(id+"F12.wireOp",EDGE,"E35");var subQ8=sQuery(id+"F12.wireOp",EDGE,"E33");var subQ10=makeQuery(id+"F12.imprint","INTERSECT",VERTEX,{"disambiguationData":[OD(0.0)],"derivedFrom":[subQ8,subQ3]});Q7=makeQuery(id+"F12.imprint","IMPRINT",FACE,{"disambiguationData":[TD([[makeQuery(id+"F12.imprint","IMPRINT",EDGE,{"disambiguationData":[TD([[subQ10,1.0]])],"derivedFrom":subQ8}),-1.0]])]});}
            var Q8;
            {var subQ0=sQuery(id+"F12.wireOp",EDGE,"E44");var subQ3=sQuery(id+"F12.wireOp",EDGE,"E35");var subQ4=makeQuery(id+"F12.imprint","INTERSECT",VERTEX,{"disambiguationData":[OD(0.0)],"derivedFrom":[subQ3,subQ0]});Q8=makeQuery(id+"F12.imprint","IMPRINT",FACE,{"disambiguationData":[TD([[makeQuery(id+"F12.imprint","IMPRINT",EDGE,{"disambiguationData":[TD([[subQ4,-1.0]])],"derivedFrom":subQ3}),1.0]])]});}
            var Q9;
            {var subQ1=sQuery(id+"F12.wireOp",EDGE,"E36");var subQ3=sQuery(id+"F12.wireOp",EDGE,"E35");var subQ5=makeQuery(id+"F12.imprint","INTERSECT",VERTEX,{"disambiguationData":[OD(0.0)],"derivedFrom":[subQ3,subQ1]});Q9=makeQuery(id+"F12.imprint","IMPRINT",FACE,{"disambiguationData":[TD([[makeQuery(id+"F12.imprint","IMPRINT",EDGE,{"disambiguationData":[TD([[subQ5,-1.0]])],"derivedFrom":subQ3}),1.0]])]});}
            var Q10;
            {var subQ0=sQuery(id+"F12.wireOp",EDGE,"E35");var subQ1=sQuery(id+"F12.wireOp",EDGE,"E33");var subQ3=makeQuery(id+"F12.imprint","INTERSECT",VERTEX,{"disambiguationData":[OD(0.0)],"derivedFrom":[subQ1,subQ0]});Q10=makeQuery(id+"F12.imprint","IMPRINT",FACE,{"disambiguationData":[TD([[makeQuery(id+"F12.imprint","IMPRINT",EDGE,{"disambiguationData":[TD([[subQ3,1.0]])],"derivedFrom":subQ1}),1.0]])]});}
            var Q11;
            {var subQ0=sQuery(id+"F12.wireOp",EDGE,"E35");var subQ1=sQuery(id+"F12.wireOp",EDGE,"E34");var subQ3=makeQuery(id+"F12.imprint","INTERSECT",VERTEX,{"disambiguationData":[OD(0.0)],"derivedFrom":[subQ1,subQ0]});Q11=makeQuery(id+"F12.imprint","IMPRINT",FACE,{"disambiguationData":[TD([[makeQuery(id+"F12.imprint","IMPRINT",EDGE,{"disambiguationData":[TD([[subQ3,-1.0]])],"derivedFrom":subQ1}),1.0]])]});}
            var Q12;
            {var subQ0=sQuery(id+"F12.wireOp",EDGE,"E42");var subQ1=sQuery(id+"F12.wireOp",EDGE,"E35");var subQ3=makeQuery(id+"F12.imprint","INTERSECT",VERTEX,{"disambiguationData":[OD(0.0)],"derivedFrom":[subQ1,subQ0]});Q12=makeQuery(id+"F12.imprint","IMPRINT",FACE,{"disambiguationData":[TD([[makeQuery(id+"F12.imprint","IMPRINT",EDGE,{"disambiguationData":[TD([[subQ3,-1.0]])],"derivedFrom":subQ1}),1.0]])]});}
            extrude(context, id + "F15", {"entities" : qUnion([Q0, Q1, Q2, Q3, Q4, Q5, Q6, Q7, Q8, Q9, Q10, Q11, Q12]), "operationType" : NewBodyOperationType.REMOVE, "endBound" : BoundingType.THROUGH_ALL, "oppositeDirection" : true, "depth" : 25 * mm});
        }
        {
            var Q0;
            Q0=makeQuery(id+"F12.imprint","IMPRINT",FACE,{"disambiguationData":[TD([[makeQuery(id+"F12.imprint","IMPRINT",EDGE,{"derivedFrom":sQuery(id+"F12.wireOp",EDGE,"E32")}),1.0]])]});
            var Q1;
            Q1=makeQuery(id+"F12.imprint","IMPRINT",FACE,{"disambiguationData":[TD([[makeQuery(id+"F12.imprint","IMPRINT",EDGE,{"derivedFrom":sQuery(id+"F12.wireOp",EDGE,"E31")}),1.0]])]});
            extrude(context, id + "F16", {"entities" : qUnion([Q0, Q1]), "operationType" : NewBodyOperationType.REMOVE, "endBound" : BoundingType.THROUGH_ALL, "oppositeDirection" : true, "depth" : 25 * mm});
        }
        {
            var Q0;
            {var subQ0=makeQuery(id+"F1.opExtrude","CAP_FACE",FACE,{"disambiguationData":[OSD([sQuery(id+"F0.wireOp",EDGE,"E1"),sQuery(id+"F0.wireOp",EDGE,"E2"),sQuery(id+"F0.wireOp",EDGE,"E3"),sQuery(id+"F0.wireOp",EDGE,"E4")])],"isStart":true});var subQ1=makeQuery(id+"F7.opPattern","COPY",FACE,{"derivedFrom":subQ0,"instanceName":"1"});Q0=makeQuery(id+"F13.boolean.opBoolean","INTERSECT",EDGE,{"derivedFrom":[makeQuery(id+"F11.opBoolean","MERGE",FACE,{"derivedFrom":[subQ0,subQ1,makeQuery(id+"F10.opPattern","COPY",FACE,{"derivedFrom":subQ0,"instanceName":"1"}),makeQuery(id+"F10.opPattern","COPY",FACE,{"derivedFrom":subQ1,"instanceName":"1"})]}),makeQuery(id+"F13.opExtrude","SWEPT_FACE",FACE,{"disambiguationData":[OSD([sQuery(id+"F12.wireOp",EDGE,"E39")])]})]});}
            var Q1;
            {var subQ0=makeQuery(id+"F1.opExtrude","CAP_FACE",FACE,{"disambiguationData":[OSD([sQuery(id+"F0.wireOp",EDGE,"E1"),sQuery(id+"F0.wireOp",EDGE,"E2"),sQuery(id+"F0.wireOp",EDGE,"E3"),sQuery(id+"F0.wireOp",EDGE,"E4")])],"isStart":true});var subQ1=makeQuery(id+"F7.opPattern","COPY",FACE,{"derivedFrom":subQ0,"instanceName":"1"});Q1=makeQuery(id+"F13.boolean.opBoolean","INTERSECT",EDGE,{"derivedFrom":[makeQuery(id+"F11.opBoolean","MERGE",FACE,{"derivedFrom":[subQ0,subQ1,makeQuery(id+"F10.opPattern","COPY",FACE,{"derivedFrom":subQ0,"instanceName":"1"}),makeQuery(id+"F10.opPattern","COPY",FACE,{"derivedFrom":subQ1,"instanceName":"1"})]}),makeQuery(id+"F13.opExtrude","SWEPT_FACE",FACE,{"disambiguationData":[OSD([sQuery(id+"F12.wireOp",EDGE,"E41")])]})]});}
            fillet(context, id + "F17", {"entities" : qUnion([Q0, Q1]), "radius" : 3 * mm, "tangentPropagation" : true, "allowEdgeOverflow" : false});
        }
        {
            var Q0;
            {var subQ0=sQuery(id+"F12.wireOp",EDGE,"E42");Q0=makeQuery(id+"F13.opExtrude","CAP_EDGE",EDGE,{"disambiguationData":[OSD([subQ0]),TDD([makeQuery(id+"F12.imprint","IMPRINT",EDGE,{"disambiguationData":[TD([[makeQuery(id+"F12.imprint","INTERSECT",VERTEX,{"derivedFrom":[sQuery(id+"F12.wireOp",EDGE,"E37"),subQ0]}),1.0]])],"derivedFrom":subQ0})])],"isStart":true});}
            var Q1;
            {var subQ0=sQuery(id+"F12.wireOp",EDGE,"E42");Q1=makeQuery(id+"F13.opExtrude","CAP_EDGE",EDGE,{"disambiguationData":[OSD([subQ0]),TDD([makeQuery(id+"F12.imprint","IMPRINT",EDGE,{"disambiguationData":[TD([[makeQuery(id+"F12.imprint","INTERSECT",VERTEX,{"derivedFrom":[sQuery(id+"F12.wireOp",EDGE,"E36"),subQ0]}),-1.0]])],"derivedFrom":subQ0})])],"isStart":true});}
            var Q2;
            {var subQ0=sQuery(id+"F12.wireOp",EDGE,"E42");var subQ2=sQuery(id+"F12.wireOp",EDGE,"E35");var subQ3=makeQuery(id+"F12.imprint","INTERSECT",VERTEX,{"disambiguationData":[OD(0.0)],"derivedFrom":[subQ2,subQ0]});var subQ5=makeQuery(id+"F12.imprint","INTERSECT",VERTEX,{"disambiguationData":[OD(0.0)],"derivedFrom":[subQ2,sQuery(id+"F12.wireOp",EDGE,"E36")]});var subQ6=sQuery(id+"F12.wireOp",EDGE,"E43");var subQ7=makeQuery(id+"F12.imprint","INTERSECT",VERTEX,{"disambiguationData":[OD(1.0)],"derivedFrom":[subQ2,subQ0]});var subQ9=makeQuery(id+"F13.opExtrude","SWEPT_EDGE",EDGE,{"disambiguationData":[OSD([subQ2,subQ0]),TDD([subQ3])]});Q2=makeQuery(id+"F15.boolean.opBoolean","MERGE",EDGE,{"derivedFrom":[makeQuery(id+"F14.boolean.opBoolean","SPLIT",EDGE,{"disambiguationData":[topologyDisambiguationEdgeConnected([makeQuery(id+"F13.opExtrude","SWEPT_FACE",FACE,{"disambiguationData":[OSD([subQ2])]})])],"derivedFrom":subQ9}),makeQuery(id+"F14.boolean.opBoolean","SPLIT",EDGE,{"disambiguationData":[topologyDisambiguationEdgeConnected([makeQuery(id+"F14.opExtrude","SWEPT_FACE",FACE,{"disambiguationData":[OSD([subQ2]),TDD([makeQuery(id+"F12.imprint","IMPRINT",EDGE,{"disambiguationData":[TD([[makeQuery(id+"F12.imprint","INTERSECT",VERTEX,{"disambiguationData":[OD(0.0)],"derivedFrom":[subQ2,subQ6]}),-1.0]])],"derivedFrom":subQ2}),makeQuery(id+"F12.imprint","IMPRINT",EDGE,{"disambiguationData":[TD([[subQ3,1.0]])],"derivedFrom":subQ2}),makeQuery(id+"F12.imprint","IMPRINT",EDGE,{"disambiguationData":[TD([[subQ3,-1.0]])],"derivedFrom":subQ2}),makeQuery(id+"F12.imprint","IMPRINT",EDGE,{"disambiguationData":[TD([[subQ7,-1.0]])],"derivedFrom":subQ2}),makeQuery(id+"F12.imprint","IMPRINT",EDGE,{"disambiguationData":[TD([[subQ5,-1.0]])],"derivedFrom":subQ2})])]})])],"derivedFrom":subQ9})]});}
            var Q3;
            {var subQ0=sQuery(id+"F12.wireOp",EDGE,"E35");var subQ1=makeQuery(id+"F12.imprint","INTERSECT",VERTEX,{"disambiguationData":[OD(1.0)],"derivedFrom":[subQ0,sQuery(id+"F12.wireOp",EDGE,"E36")]});var subQ2=sQuery(id+"F12.wireOp",EDGE,"E44");var subQ6=makeQuery(id+"F12.imprint","INTERSECT",VERTEX,{"derivedFrom":[subQ0,sQuery(id+"F12.wireOp",EDGE,"E40")]});var subQ8=makeQuery(id+"F12.imprint","INTERSECT",VERTEX,{"disambiguationData":[OD(1.0)],"derivedFrom":[subQ0,sQuery(id+"F12.wireOp",EDGE,"E37")]});Q3=makeQuery(id+"F14.boolean.opBoolean","COPY",EDGE,{"derivedFrom":makeQuery(id+"F14.opExtrude","CAP_EDGE",EDGE,{"disambiguationData":[OSD([subQ0]),TDD([makeQuery(id+"F12.imprint","IMPRINT",EDGE,{"disambiguationData":[TD([[makeQuery(id+"F12.imprint","INTERSECT",VERTEX,{"disambiguationData":[OD(0.0)],"derivedFrom":[subQ0,subQ2]}),-1.0]])],"derivedFrom":subQ0}),makeQuery(id+"F12.imprint","IMPRINT",EDGE,{"disambiguationData":[TD([[subQ1,-1.0]])],"derivedFrom":subQ0}),makeQuery(id+"F12.imprint","IMPRINT",EDGE,{"disambiguationData":[TD([[subQ6,1.0]])],"derivedFrom":subQ0}),makeQuery(id+"F12.imprint","IMPRINT",EDGE,{"disambiguationData":[TD([[subQ6,-1.0]])],"derivedFrom":subQ0}),makeQuery(id+"F12.imprint","IMPRINT",EDGE,{"disambiguationData":[TD([[subQ8,1.0]])],"derivedFrom":subQ0}),makeQuery(id+"F12.imprint","IMPRINT",EDGE,{"disambiguationData":[TD([[subQ8,-1.0]])],"derivedFrom":subQ0})])],"isStart":true})});}
            var Q4;
            {var subQ0=sQuery(id+"F12.wireOp",EDGE,"E35");var subQ2=sQuery(id+"F12.wireOp",EDGE,"E43");var subQ3=sQuery(id+"F12.wireOp",EDGE,"E42");var subQ4=makeQuery(id+"F12.imprint","INTERSECT",VERTEX,{"disambiguationData":[OD(0.0)],"derivedFrom":[subQ0,subQ3]});var subQ5=makeQuery(id+"F12.imprint","INTERSECT",VERTEX,{"disambiguationData":[OD(1.0)],"derivedFrom":[subQ0,subQ3]});var subQ6=makeQuery(id+"F12.imprint","INTERSECT",VERTEX,{"disambiguationData":[OD(0.0)],"derivedFrom":[subQ0,sQuery(id+"F12.wireOp",EDGE,"E36")]});Q4=makeQuery(id+"F14.boolean.opBoolean","COPY",EDGE,{"disambiguationData":[OD(0.0)],"derivedFrom":makeQuery(id+"F14.opExtrude","CAP_EDGE",EDGE,{"disambiguationData":[OSD([subQ0]),TDD([makeQuery(id+"F12.imprint","IMPRINT",EDGE,{"disambiguationData":[TD([[makeQuery(id+"F12.imprint","INTERSECT",VERTEX,{"disambiguationData":[OD(0.0)],"derivedFrom":[subQ0,subQ2]}),-1.0]])],"derivedFrom":subQ0}),makeQuery(id+"F12.imprint","IMPRINT",EDGE,{"disambiguationData":[TD([[subQ4,1.0]])],"derivedFrom":subQ0}),makeQuery(id+"F12.imprint","IMPRINT",EDGE,{"disambiguationData":[TD([[subQ4,-1.0]])],"derivedFrom":subQ0}),makeQuery(id+"F12.imprint","IMPRINT",EDGE,{"disambiguationData":[TD([[subQ5,-1.0]])],"derivedFrom":subQ0}),makeQuery(id+"F12.imprint","IMPRINT",EDGE,{"disambiguationData":[TD([[subQ6,-1.0]])],"derivedFrom":subQ0})])],"isStart":true})});}
            var Q5;
            Q5=makeQuery(id+"F3.opExtrude","CAP_EDGE",EDGE,{"disambiguationData":[OSD([sQuery(id+"F2.wireOp",EDGE,"E20")])],"isStart":false});
            var Q6;
            Q6=makeQuery(id+"F7.opPattern","COPY",EDGE,{"derivedFrom":makeQuery(id+"F3.opExtrude","CAP_EDGE",EDGE,{"disambiguationData":[OSD([sQuery(id+"F2.wireOp",EDGE,"E20")])],"isStart":false}),"instanceName":"1"});
            var Q7;
            Q7=makeQuery(id+"F10.opPattern","COPY",EDGE,{"derivedFrom":makeQuery(id+"F7.opPattern","COPY",EDGE,{"derivedFrom":makeQuery(id+"F3.opExtrude","CAP_EDGE",EDGE,{"disambiguationData":[OSD([sQuery(id+"F2.wireOp",EDGE,"E20")])],"isStart":false}),"instanceName":"1"}),"instanceName":"1"});
            var Q8;
            Q8=makeQuery(id+"F10.opPattern","COPY",EDGE,{"derivedFrom":makeQuery(id+"F3.opExtrude","CAP_EDGE",EDGE,{"disambiguationData":[OSD([sQuery(id+"F2.wireOp",EDGE,"E20")])],"isStart":false}),"instanceName":"1"});
            var Q9;
            {var subQ0=makeQuery(id+"F1.opExtrude","CAP_EDGE",EDGE,{"disambiguationData":[OSD([sQuery(id+"F0.wireOp",EDGE,"E3")])],"isStart":false});Q9=makeQuery(id+"F11.opBoolean","MERGE",EDGE,{"derivedFrom":[subQ0,makeQuery(id+"F10.opPattern","COPY",EDGE,{"derivedFrom":subQ0,"instanceName":"1"})]});}
            var Q10;
            {var subQ0=makeQuery(id+"F6.boolean.opBoolean","INTERSECT",EDGE,{"derivedFrom":[makeQuery(id+"F1.opExtrude","CAP_FACE",FACE,{"disambiguationData":[OSD([sQuery(id+"F0.wireOp",EDGE,"E1"),sQuery(id+"F0.wireOp",EDGE,"E2"),sQuery(id+"F0.wireOp",EDGE,"E3"),sQuery(id+"F0.wireOp",EDGE,"E4")])],"isStart":true}),makeQuery(id+"F6.opExtrude","SWEPT_FACE",FACE,{"disambiguationData":[OSD([sQuery(id+"F0.wireOp",EDGE,"E0")])]})]});Q10=makeQuery(id+"F11.opBoolean","MERGE",EDGE,{"derivedFrom":[makeQuery(id+"F10.opPattern","COPY",EDGE,{"derivedFrom":subQ0,"instanceName":"1"}),makeQuery(id+"F10.opPattern","COPY",EDGE,{"derivedFrom":makeQuery(id+"F7.opPattern","COPY",EDGE,{"derivedFrom":subQ0,"instanceName":"1"}),"instanceName":"1"})]});}
            var Q11;
            {var subQ0=makeQuery(id+"F6.boolean.opBoolean","INTERSECT",EDGE,{"derivedFrom":[makeQuery(id+"F1.opExtrude","CAP_FACE",FACE,{"disambiguationData":[OSD([sQuery(id+"F0.wireOp",EDGE,"E1"),sQuery(id+"F0.wireOp",EDGE,"E2"),sQuery(id+"F0.wireOp",EDGE,"E3"),sQuery(id+"F0.wireOp",EDGE,"E4")])],"isStart":true}),makeQuery(id+"F6.opExtrude","SWEPT_FACE",FACE,{"disambiguationData":[OSD([sQuery(id+"F0.wireOp",EDGE,"E0")])]})]});Q11=makeQuery(id+"F11.opBoolean","MERGE",EDGE,{"derivedFrom":[subQ0,makeQuery(id+"F7.opPattern","COPY",EDGE,{"derivedFrom":subQ0,"instanceName":"1"})]});}
            var Q12;
            {var subQ0=makeQuery(id+"F6.boolean.opBoolean","INTERSECT",EDGE,{"derivedFrom":[makeQuery(id+"F1.opExtrude","CAP_FACE",FACE,{"disambiguationData":[OSD([sQuery(id+"F0.wireOp",EDGE,"E1"),sQuery(id+"F0.wireOp",EDGE,"E2"),sQuery(id+"F0.wireOp",EDGE,"E3"),sQuery(id+"F0.wireOp",EDGE,"E4")])],"isStart":false}),makeQuery(id+"F6.opExtrude","SWEPT_FACE",FACE,{"disambiguationData":[OSD([sQuery(id+"F0.wireOp",EDGE,"E0")])]})]});Q12=makeQuery(id+"F11.opBoolean","MERGE",EDGE,{"derivedFrom":[subQ0,makeQuery(id+"F7.opPattern","COPY",EDGE,{"derivedFrom":subQ0,"instanceName":"1"})]});}
            var Q13;
            {var subQ0=makeQuery(id+"F6.boolean.opBoolean","INTERSECT",EDGE,{"derivedFrom":[makeQuery(id+"F1.opExtrude","CAP_FACE",FACE,{"disambiguationData":[OSD([sQuery(id+"F0.wireOp",EDGE,"E1"),sQuery(id+"F0.wireOp",EDGE,"E2"),sQuery(id+"F0.wireOp",EDGE,"E3"),sQuery(id+"F0.wireOp",EDGE,"E4")])],"isStart":false}),makeQuery(id+"F6.opExtrude","SWEPT_FACE",FACE,{"disambiguationData":[OSD([sQuery(id+"F0.wireOp",EDGE,"E0")])]})]});Q13=makeQuery(id+"F11.opBoolean","MERGE",EDGE,{"derivedFrom":[makeQuery(id+"F10.opPattern","COPY",EDGE,{"derivedFrom":subQ0,"instanceName":"1"}),makeQuery(id+"F10.opPattern","COPY",EDGE,{"derivedFrom":makeQuery(id+"F7.opPattern","COPY",EDGE,{"derivedFrom":subQ0,"instanceName":"1"}),"instanceName":"1"})]});}
            var Q14;
            {var subQ0=sQuery(id+"F12.wireOp",EDGE,"E35");var subQ1=makeQuery(id+"F7.opPattern","COPY",FACE,{"derivedFrom":makeQuery(id+"F3.boolean.opBoolean","MERGE",FACE,{"derivedFrom":[makeQuery(id+"F1.opExtrude","SWEPT_FACE",FACE,{"disambiguationData":[OSD([sQuery(id+"F0.wireOp",EDGE,"E3")])]}),makeQuery(id+"F3.opExtrude","CAP_FACE",FACE,{"disambiguationData":[OSD([sQuery(id+"F2.wireOp",EDGE,"E20"),sQuery(id+"F2.wireOp",EDGE,"E24"),sQuery(id+"F2.wireOp",EDGE,"E25"),sQuery(id+"F2.wireOp",EDGE,"E26")])],"isStart":false})]}),"instanceName":"1"});Q14=makeQuery(id+"F15.boolean.opBoolean","INTERSECT",EDGE,{"derivedFrom":[makeQuery(id+"F13.boolean.opBoolean","MERGE",FACE,{"derivedFrom":[makeQuery(id+"F11.opBoolean","MERGE",FACE,{"derivedFrom":[subQ1,makeQuery(id+"F10.opPattern","COPY",FACE,{"derivedFrom":subQ1,"instanceName":"1"})]}),makeQuery(id+"F13.opExtrude","CAP_FACE",FACE,{"disambiguationData":[OSD([subQ0,sQuery(id+"F12.wireOp",EDGE,"E36"),sQuery(id+"F12.wireOp",EDGE,"E37"),sQuery(id+"F12.wireOp",EDGE,"E39"),sQuery(id+"F12.wireOp",EDGE,"E40"),sQuery(id+"F12.wireOp",EDGE,"E41"),sQuery(id+"F12.wireOp",EDGE,"E42")])],"isStart":false})]}),makeQuery(id+"F15.opExtrude","SWEPT_FACE",FACE,{"disambiguationData":[OSD([subQ0])]})]});}
            var Q15;
            {var subQ0=sQuery(id+"F12.wireOp",EDGE,"E42");var subQ1=sQuery(id+"F12.wireOp",EDGE,"E36");var subQ2=sQuery(id+"F12.wireOp",EDGE,"E35");var subQ3=makeQuery(id+"F12.imprint","INTERSECT",VERTEX,{"disambiguationData":[OD(1.0)],"derivedFrom":[subQ2,subQ0]});var subQ5=makeQuery(id+"F12.imprint","INTERSECT",VERTEX,{"disambiguationData":[OD(0.0)],"derivedFrom":[subQ2,subQ1]});var subQ6=sQuery(id+"F12.wireOp",EDGE,"E43");var subQ7=makeQuery(id+"F12.imprint","INTERSECT",VERTEX,{"disambiguationData":[OD(0.0)],"derivedFrom":[subQ2,subQ0]});var subQ9=makeQuery(id+"F13.opExtrude","SWEPT_EDGE",EDGE,{"disambiguationData":[OSD([subQ2,subQ0]),TDD([subQ3])]});Q15=makeQuery(id+"F15.boolean.opBoolean","MERGE",EDGE,{"derivedFrom":[makeQuery(id+"F14.boolean.opBoolean","SPLIT",EDGE,{"disambiguationData":[topologyDisambiguationEdgeConnected([makeQuery(id+"F13.opExtrude","SWEPT_FACE",FACE,{"disambiguationData":[OSD([subQ2])]})])],"derivedFrom":subQ9}),makeQuery(id+"F14.boolean.opBoolean","SPLIT",EDGE,{"disambiguationData":[topologyDisambiguationEdgeConnected([makeQuery(id+"F14.opExtrude","SWEPT_FACE",FACE,{"disambiguationData":[OSD([subQ2]),TDD([makeQuery(id+"F12.imprint","IMPRINT",EDGE,{"disambiguationData":[TD([[makeQuery(id+"F12.imprint","INTERSECT",VERTEX,{"disambiguationData":[OD(0.0)],"derivedFrom":[subQ2,subQ6]}),-1.0]])],"derivedFrom":subQ2}),makeQuery(id+"F12.imprint","IMPRINT",EDGE,{"disambiguationData":[TD([[subQ7,1.0]])],"derivedFrom":subQ2}),makeQuery(id+"F12.imprint","IMPRINT",EDGE,{"disambiguationData":[TD([[subQ7,-1.0]])],"derivedFrom":subQ2}),makeQuery(id+"F12.imprint","IMPRINT",EDGE,{"disambiguationData":[TD([[subQ3,-1.0]])],"derivedFrom":subQ2}),makeQuery(id+"F12.imprint","IMPRINT",EDGE,{"disambiguationData":[TD([[subQ5,-1.0]])],"derivedFrom":subQ2})])]})])],"derivedFrom":subQ9})]});}
            var Q16;
            {var subQ0=sQuery(id+"F12.wireOp",EDGE,"E35");var subQ2=sQuery(id+"F12.wireOp",EDGE,"E43");var subQ3=sQuery(id+"F12.wireOp",EDGE,"E42");var subQ4=makeQuery(id+"F12.imprint","INTERSECT",VERTEX,{"disambiguationData":[OD(0.0)],"derivedFrom":[subQ0,subQ3]});var subQ5=makeQuery(id+"F12.imprint","INTERSECT",VERTEX,{"disambiguationData":[OD(1.0)],"derivedFrom":[subQ0,subQ3]});var subQ6=makeQuery(id+"F12.imprint","INTERSECT",VERTEX,{"disambiguationData":[OD(0.0)],"derivedFrom":[subQ0,sQuery(id+"F12.wireOp",EDGE,"E36")]});Q16=makeQuery(id+"F14.boolean.opBoolean","COPY",EDGE,{"disambiguationData":[OD(1.0)],"derivedFrom":makeQuery(id+"F14.opExtrude","CAP_EDGE",EDGE,{"disambiguationData":[OSD([subQ0]),TDD([makeQuery(id+"F12.imprint","IMPRINT",EDGE,{"disambiguationData":[TD([[makeQuery(id+"F12.imprint","INTERSECT",VERTEX,{"disambiguationData":[OD(0.0)],"derivedFrom":[subQ0,subQ2]}),-1.0]])],"derivedFrom":subQ0}),makeQuery(id+"F12.imprint","IMPRINT",EDGE,{"disambiguationData":[TD([[subQ4,1.0]])],"derivedFrom":subQ0}),makeQuery(id+"F12.imprint","IMPRINT",EDGE,{"disambiguationData":[TD([[subQ4,-1.0]])],"derivedFrom":subQ0}),makeQuery(id+"F12.imprint","IMPRINT",EDGE,{"disambiguationData":[TD([[subQ5,-1.0]])],"derivedFrom":subQ0}),makeQuery(id+"F12.imprint","IMPRINT",EDGE,{"disambiguationData":[TD([[subQ6,-1.0]])],"derivedFrom":subQ0})])],"isStart":true})});}
            fillet(context, id + "F18", {"entities" : qUnion([Q0, Q1, Q2, Q3, Q4, Q5, Q6, Q7, Q8, Q9, Q10, Q11, Q12, Q13, Q14, Q15, Q16]), "radius" : 1 * mm, "tangentPropagation" : true, "allowEdgeOverflow" : false});
        }
    });
